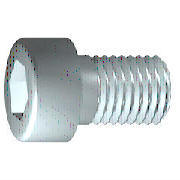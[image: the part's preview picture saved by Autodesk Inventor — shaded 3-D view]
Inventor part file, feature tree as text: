
AUTODESK INVENTOR PART (.ipt)
format: ipt  version: 2022 (Build 260153000, 153)  size: 186,880 bytes
history: native  units: mm (DEFAULTED — no unit token found)
features: sketch x2, other x1, extrude x1, plane x1, fillet x1
ambient origin geometry x7: Origin, YZ Plane, XY Plane, X Axis, Y Axis, Z Axis, Center Point
bodies: Solid1 (feature_tree)
feature tree (6):
  other  "Базовый элемент"
  extrude  "Паз"  Depth=20.0mm
  plane  "Work Plane1"
  fillet  "Fillet2"  Radius=0.429515mm
  sketch  "Эскиз1"
  sketch  "Эскиз2"
